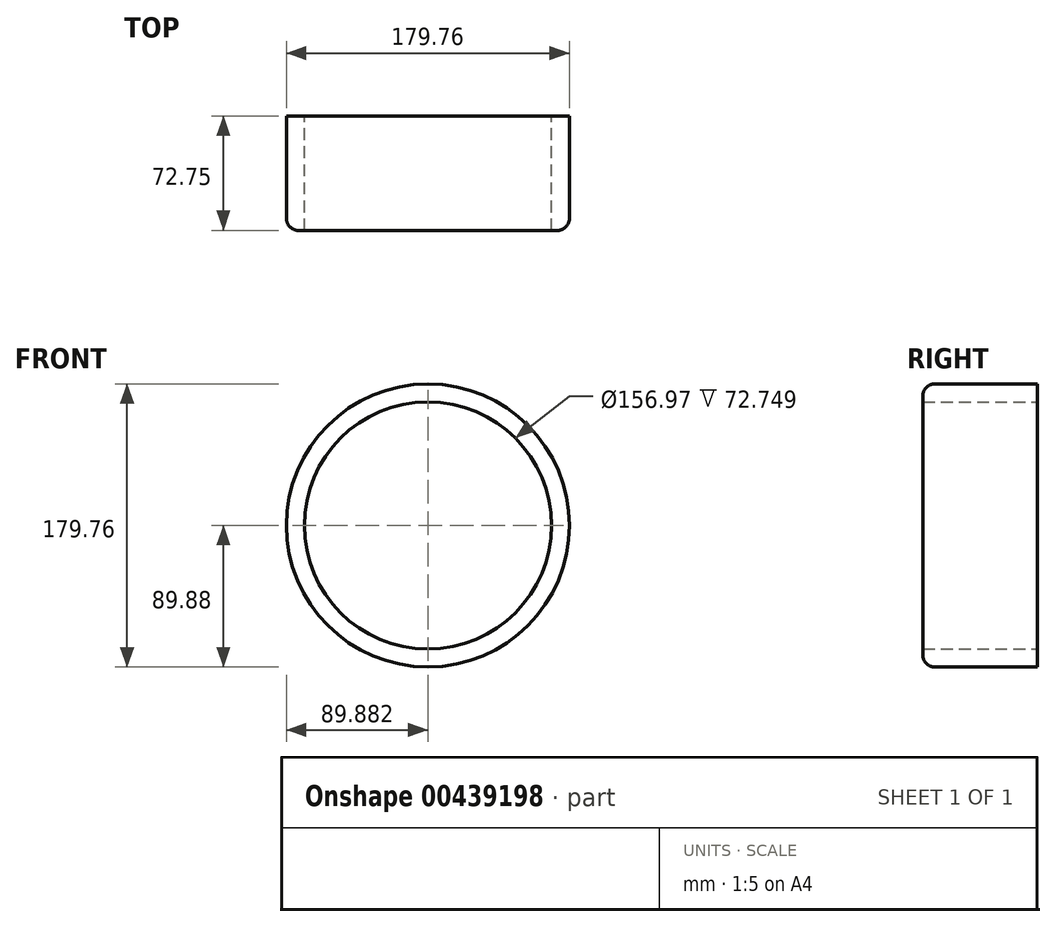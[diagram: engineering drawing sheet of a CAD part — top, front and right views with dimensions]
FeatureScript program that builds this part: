
annotation { "Feature Type Name" : "Feature", "Feature Type Description" : "" }
export const myFeature = defineFeature(function(context is Context, id is Id, definition is map)
    precondition{}
    {
        {
            var Q0;
            Q0=qCreatedBy(makeId("Top.planeOp"),FACE);
            var sketch = newSketch(context, id + "F0", { "sketchPlane" : qUnion([Q0])});
            skLineSegment(sketch, "E0", {"start": v(-97.88, -7.77) * mm, "end": v(-109.27, -7.77) * mm});
            skLineSegment(sketch, "E1", {"start": v(-97.88, -7.77) * mm, "end": v(-97.88, 64.98) * mm});
            skLineSegment(sketch, "E2", {"start": v(-109.27, 64.98) * mm, "end": v(-97.88, 64.98) * mm});
            skLineSegment(sketch, "E3", {"start": v(-109.27, 64.98) * mm, "end": v(-109.27, -7.77) * mm});
            skLineSegment(sketch, "E4", {"start": v(-19.39, 95) * mm, "end": v(-19.39, -23.98) * mm, "construction": true});
            skSolve(sketch);
        }
        {
            var Q0;
            Q0=makeQuery(id+"F0.imprint","IMPRINT",FACE,{"disambiguationData":[TD([[makeQuery(id+"F0.imprint","IMPRINT",EDGE,{"derivedFrom":sQuery(id+"F0.wireOp",EDGE,"E0")}),-1.0]])]});
            var Q1;
            Q1=sQuery(id+"F0.wireOp",EDGE,"E4");
            var Q2;
            Q2=sQuery(id+"F0.wireOp",EDGE,"E4");
            revolve(context, id + "F1", {"entities" : qUnion([Q0]), "surfaceEntities" : qUnion([Q1]), "axis" : qUnion([Q2]), "revolveType" : RevolveType.FULL});
        }
        {
            var Q0;
            Q0=makeQuery(id+"F1.opRevolve","SWEPT_EDGE",EDGE,{"disambiguationData":[OSD([sQuery(id+"F0.wireOp",EDGE,"E0"),sQuery(id+"F0.wireOp",EDGE,"E3")])]});
            fillet(context, id + "F2", {"entities" : qUnion([Q0]), "radius" : 7.62 * mm, "tangentPropagation" : true, "allowEdgeOverflow" : false});
        }
    });
